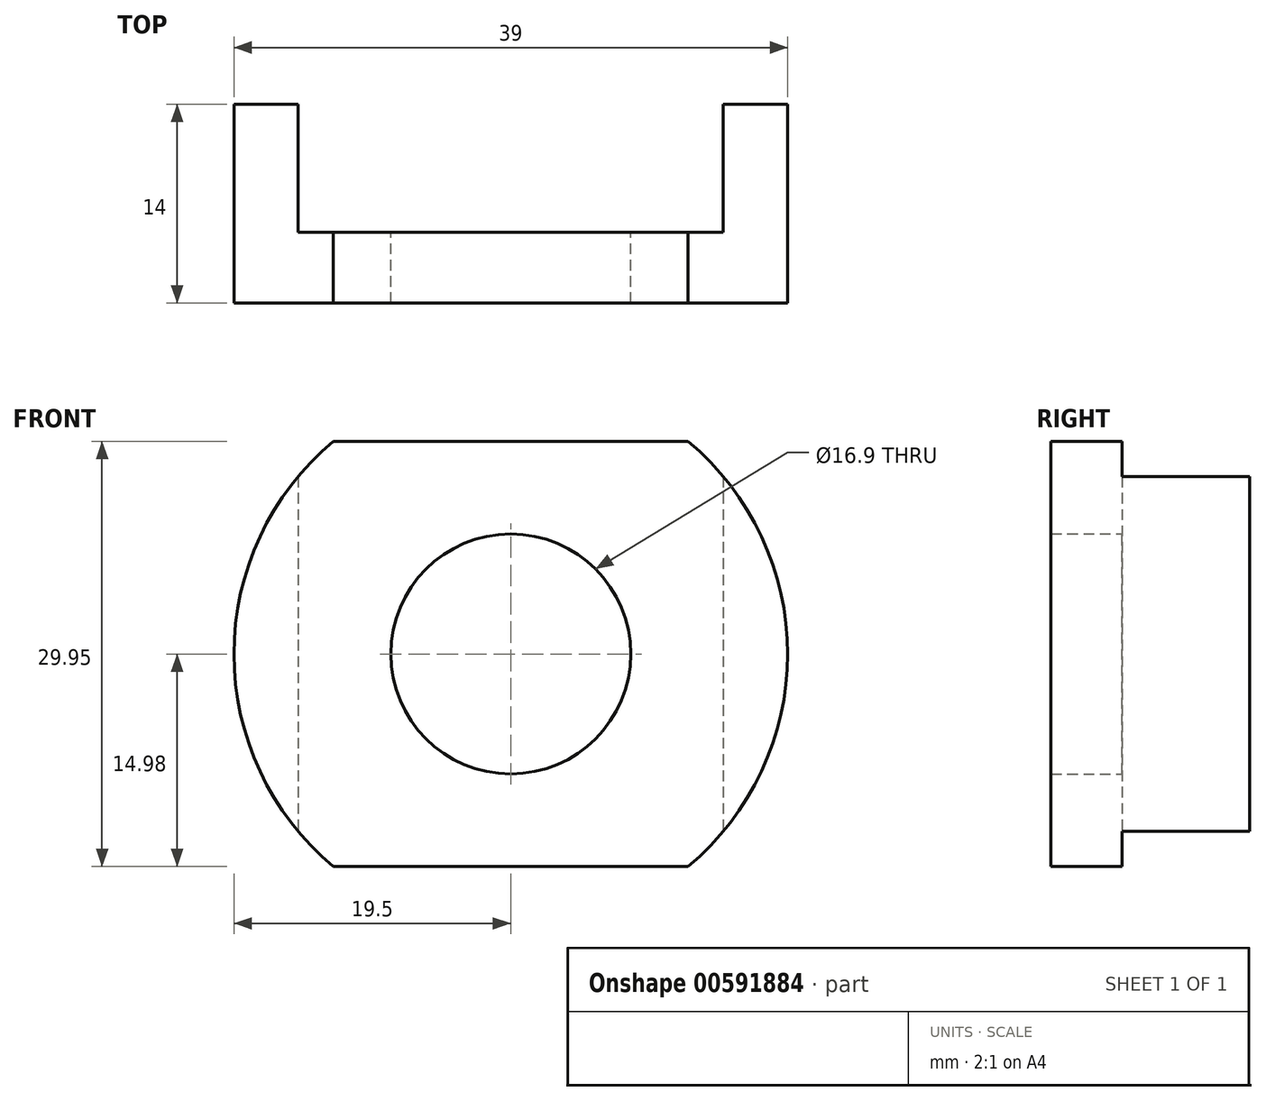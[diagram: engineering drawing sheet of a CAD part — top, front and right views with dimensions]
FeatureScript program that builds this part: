
annotation { "Feature Type Name" : "Feature", "Feature Type Description" : "" }
export const myFeature = defineFeature(function(context is Context, id is Id, definition is map)
    precondition{}
    {
        {
            var Q0;
            Q0=qCreatedBy(makeId("Front.planeOp"),FACE);
            var sketch = newSketch(context, id + "F0", { "sketchPlane" : qUnion([Q0])});
            skLineSegment(sketch, "E0.bottom", {"start": v(14.98, 14.97) * mm, "end": v(-14.97, 14.97) * mm});
            skLineSegment(sketch, "E0.top", {"start": v(14.97, -14.97) * mm, "end": v(-14.98, -14.97) * mm});
            skLineSegment(sketch, "E0.left", {"start": v(14.98, 14.98) * mm, "end": v(14.97, -14.97) * mm});
            skLineSegment(sketch, "E0.right", {"start": v(-14.97, 14.97) * mm, "end": v(-14.98, -14.97) * mm});
            skPoint(sketch, "E0.middle", {"position": v(0, 0) * mm});
            skCircle(sketch, "E1", {"center": v(0, 0) * mm, "radius": 19.5 * mm});
            skCircle(sketch, "E2", {"center": v(0, 0) * mm, "radius": 8.45 * mm});
            skSolve(sketch);
        }
        {
            var Q0;
            Q0=makeQuery(id+"F0.imprint","IMPRINT",FACE,{"disambiguationData":[TD([[makeQuery(id+"F0.imprint","IMPRINT",EDGE,{"derivedFrom":sQuery(id+"F0.wireOp",EDGE,"E2")}),-1.0]])]});
            var Q1;
            {var subQ0=sQuery(id+"F0.wireOp",EDGE,"E1");var subQ1=sQuery(id+"F0.wireOp",EDGE,"E0.bottom");var subQ2=makeQuery(id+"F0.imprint","INTERSECT",VERTEX,{"disambiguationData":[OD(0.0)],"derivedFrom":[subQ1,subQ0]});Q1=makeQuery(id+"F0.imprint","IMPRINT",FACE,{"disambiguationData":[TD([[makeQuery(id+"F0.imprint","IMPRINT",EDGE,{"disambiguationData":[TD([[subQ2,-1.0]])],"derivedFrom":subQ1}),-1.0]])]});}
            var Q2;
            {var subQ0=sQuery(id+"F0.wireOp",EDGE,"E1");var subQ1=sQuery(id+"F0.wireOp",EDGE,"E0.top");var subQ2=makeQuery(id+"F0.imprint","INTERSECT",VERTEX,{"disambiguationData":[OD(0.0)],"derivedFrom":[subQ1,subQ0]});Q2=makeQuery(id+"F0.imprint","IMPRINT",FACE,{"disambiguationData":[TD([[makeQuery(id+"F0.imprint","IMPRINT",EDGE,{"disambiguationData":[TD([[subQ2,-1.0]])],"derivedFrom":subQ1}),1.0]])]});}
            var Q3;
            {var subQ0=sQuery(id+"F0.wireOp",EDGE,"E1");var subQ1=sQuery(id+"F0.wireOp",EDGE,"E0.left");var subQ2=makeQuery(id+"F0.imprint","INTERSECT",VERTEX,{"disambiguationData":[OD(0.0)],"derivedFrom":[subQ1,subQ0]});Q3=makeQuery(id+"F0.imprint","IMPRINT",FACE,{"disambiguationData":[TD([[makeQuery(id+"F0.imprint","IMPRINT",EDGE,{"disambiguationData":[TD([[subQ2,-1.0]])],"derivedFrom":subQ1}),1.0]])]});}
            var Q4;
            {var subQ0=sQuery(id+"F0.wireOp",EDGE,"E1");var subQ1=sQuery(id+"F0.wireOp",EDGE,"E0.right");var subQ2=makeQuery(id+"F0.imprint","INTERSECT",VERTEX,{"disambiguationData":[OD(0.0)],"derivedFrom":[subQ1,subQ0]});Q4=makeQuery(id+"F0.imprint","IMPRINT",FACE,{"disambiguationData":[TD([[makeQuery(id+"F0.imprint","IMPRINT",EDGE,{"disambiguationData":[TD([[subQ2,-1.0]])],"derivedFrom":subQ1}),-1.0]])]});}
            extrude(context, id + "F1", {"entities" : qUnion([Q0, Q1, Q2, Q3, Q4]), "depth" : 5 * mm, "offsetDistance" : 25 * mm});
        }
        {
            var Q0;
            Q0=makeQuery(id+"F1.opExtrude","CAP_FACE",FACE,{"disambiguationData":[OSD([sQuery(id+"F0.wireOp",EDGE,"E1"),sQuery(id+"F0.wireOp",EDGE,"E2")])],"isStart":true});
            var sketch = newSketch(context, id + "F2", { "sketchPlane" : qUnion([Q0])});
            skLineSegment(sketch, "E3.bottom", {"start": v(-14.97, 14.97) * mm, "end": v(14.98, 14.97) * mm});
            skLineSegment(sketch, "E3.top", {"start": v(-14.98, -14.98) * mm, "end": v(14.97, -14.98) * mm});
            skLineSegment(sketch, "E3.left", {"start": v(-14.97, 14.98) * mm, "end": v(-14.98, -14.98) * mm});
            skLineSegment(sketch, "E3.right", {"start": v(14.98, 14.98) * mm, "end": v(14.97, -14.98) * mm});
            skPoint(sketch, "E3.middle", {"position": v(0, 0) * mm});
            skCircle(sketch, "E4", {"center": v(0, 0) * mm, "radius": 19.5 * mm});
            skSolve(sketch);
        }
        {
            var Q0;
            {var subQ0=sQuery(id+"F2.wireOp",EDGE,"E4");var subQ1=sQuery(id+"F2.wireOp",EDGE,"E3.bottom");var subQ2=makeQuery(id+"F2.imprint","INTERSECT",VERTEX,{"disambiguationData":[OD(0.0)],"derivedFrom":[subQ1,subQ0]});Q0=makeQuery(id+"F2.imprint","IMPRINT",FACE,{"disambiguationData":[TD([[makeQuery(id+"F2.imprint","IMPRINT",EDGE,{"disambiguationData":[TD([[subQ2,-1.0]])],"derivedFrom":subQ1}),1.0]])]});}
            var Q1;
            {var subQ0=sQuery(id+"F2.wireOp",EDGE,"E4");var subQ1=sQuery(id+"F2.wireOp",EDGE,"E3.top");var subQ2=makeQuery(id+"F2.imprint","INTERSECT",VERTEX,{"disambiguationData":[OD(0.0)],"derivedFrom":[subQ1,subQ0]});Q1=makeQuery(id+"F2.imprint","IMPRINT",FACE,{"disambiguationData":[TD([[makeQuery(id+"F2.imprint","IMPRINT",EDGE,{"disambiguationData":[TD([[subQ2,-1.0]])],"derivedFrom":subQ1}),-1.0]])]});}
            extrude(context, id + "F3", {"entities" : qUnion([Q0, Q1]), "operationType" : NewBodyOperationType.REMOVE, "endBound" : BoundingType.UP_TO_NEXT, "oppositeDirection" : true, "depth" : 5 * mm, "offsetDistance" : 25 * mm});
        }
        {
            var Q0;
            Q0=makeQuery(id+"F1.opExtrude","CAP_FACE",FACE,{"disambiguationData":[OSD([sQuery(id+"F0.wireOp",EDGE,"E1"),sQuery(id+"F0.wireOp",EDGE,"E2")])],"isStart":true});
            var sketch = newSketch(context, id + "F4", { "sketchPlane" : qUnion([Q0])});
            skLineSegment(sketch, "E5.bottom", {"start": v(-14.97, 14.98) * mm, "end": v(14.98, 14.98) * mm});
            skLineSegment(sketch, "E5.top", {"start": v(-14.98, -14.97) * mm, "end": v(14.97, -14.97) * mm});
            skLineSegment(sketch, "E5.left", {"start": v(-14.97, 14.98) * mm, "end": v(-14.98, -14.97) * mm});
            skLineSegment(sketch, "E5.right", {"start": v(14.98, 14.98) * mm, "end": v(14.97, -14.97) * mm});
            skPoint(sketch, "E5.middle", {"position": v(0, 0) * mm});
            skSolve(sketch);
        }
        {
            var Q0;
            {var subQ0=sQuery(id+"F4.wireOp",EDGE,"E5.left");var subQ1=makeQuery(id+"F3.boolean.opBoolean","SPLIT",EDGE,{"disambiguationData":[OD(0.0)],"derivedFrom":makeQuery(id+"F1.opExtrude","CAP_EDGE",EDGE,{"disambiguationData":[OSD([sQuery(id+"F0.wireOp",EDGE,"E1")])],"isStart":true})});var subQ2=makeQuery(id+"F4.imprint","INTERSECT",VERTEX,{"disambiguationData":[OD(0.0)],"derivedFrom":[subQ1,subQ0]});Q0=makeQuery(id+"F4.imprint","IMPRINT",FACE,{"disambiguationData":[TD([[makeQuery(id+"F4.imprint","IMPRINT",EDGE,{"disambiguationData":[TD([[subQ2,-1.0]])],"derivedFrom":subQ0}),-1.0]])]});}
            var Q1;
            {var subQ0=sQuery(id+"F4.wireOp",EDGE,"E5.right");var subQ1=makeQuery(id+"F3.boolean.opBoolean","SPLIT",EDGE,{"disambiguationData":[OD(1.0)],"derivedFrom":makeQuery(id+"F1.opExtrude","CAP_EDGE",EDGE,{"disambiguationData":[OSD([sQuery(id+"F0.wireOp",EDGE,"E1")])],"isStart":true})});var subQ2=makeQuery(id+"F4.imprint","INTERSECT",VERTEX,{"disambiguationData":[OD(0.0)],"derivedFrom":[subQ1,subQ0]});Q1=makeQuery(id+"F4.imprint","IMPRINT",FACE,{"disambiguationData":[TD([[makeQuery(id+"F4.imprint","IMPRINT",EDGE,{"disambiguationData":[TD([[subQ2,-1.0]])],"derivedFrom":subQ0}),1.0]])]});}
            extrude(context, id + "F5", {"entities" : qUnion([Q0, Q1]), "operationType" : NewBodyOperationType.ADD, "depth" : 9 * mm, "offsetDistance" : 25 * mm});
        }
    });
